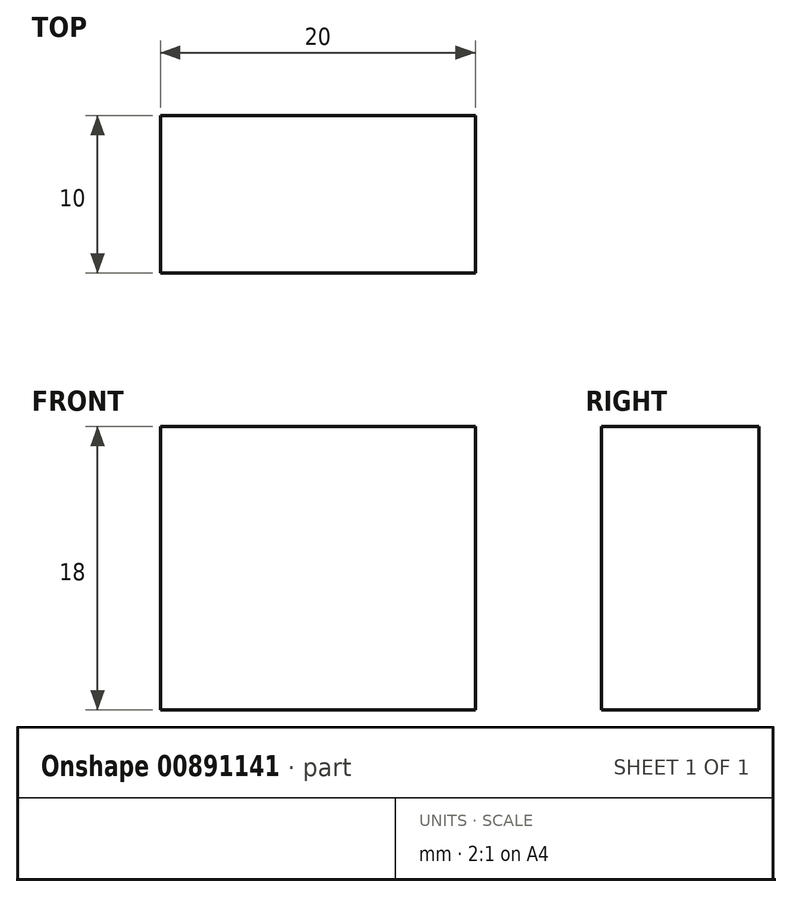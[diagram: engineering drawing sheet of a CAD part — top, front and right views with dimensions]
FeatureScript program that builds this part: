
annotation { "Feature Type Name" : "Feature", "Feature Type Description" : "" }
export const myFeature = defineFeature(function(context is Context, id is Id, definition is map)
    precondition{}
    {
        {
            var Q0;
            Q0=qCreatedBy(makeId("Front.planeOp"),FACE);
            var sketch = newSketch(context, id + "F0", { "sketchPlane" : qUnion([Q0])});
            skLineSegment(sketch, "E0.bottom", {"start": v(-10, -9) * mm, "end": v(10, -9) * mm});
            skLineSegment(sketch, "E0.top", {"start": v(-10, 9) * mm, "end": v(10, 9) * mm});
            skLineSegment(sketch, "E0.left", {"start": v(-10, -9) * mm, "end": v(-10, 9) * mm});
            skLineSegment(sketch, "E0.right", {"start": v(10, -9) * mm, "end": v(10, 9) * mm});
            skPoint(sketch, "E0.middle", {"position": v(0, 0) * mm});
            skSolve(sketch);
        }
        {
            var Q0;
            Q0 = qSketchRegion(id + "F0", true);
            extrude(context, id + "F1", {"entities" : qUnion([Q0]), "endBound" : BoundingType.SYMMETRIC, "depth" : 10 * mm, "offsetDistance" : 25 * mm});
        }
    });
